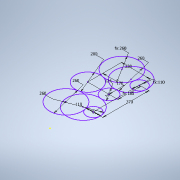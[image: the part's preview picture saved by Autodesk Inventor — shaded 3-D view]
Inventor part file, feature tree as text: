
AUTODESK INVENTOR PART (.ipt)
format: ipt  version: 2021 (Build 250183000, 183)  size: 100,864 bytes
history: native  units: mm
features: sketch x1
ambient origin geometry x8: Origin, YZ Plane, XZ Plane, XY Plane, X Axis, Y Axis, Z Axis, Center Point
feature tree (1):
  sketch  "Sketch1"  dims[d0=200.0mm d1=124.0mm d2=170.0mm d3=110.0mm d4=110.0mm d5=370.0mm d6=185.0mm d7=260.0mm d8=230.0mm d9=0.0mm d10=260.0mm d11=0.0mm d12=260.0mm d13=260.0mm]
